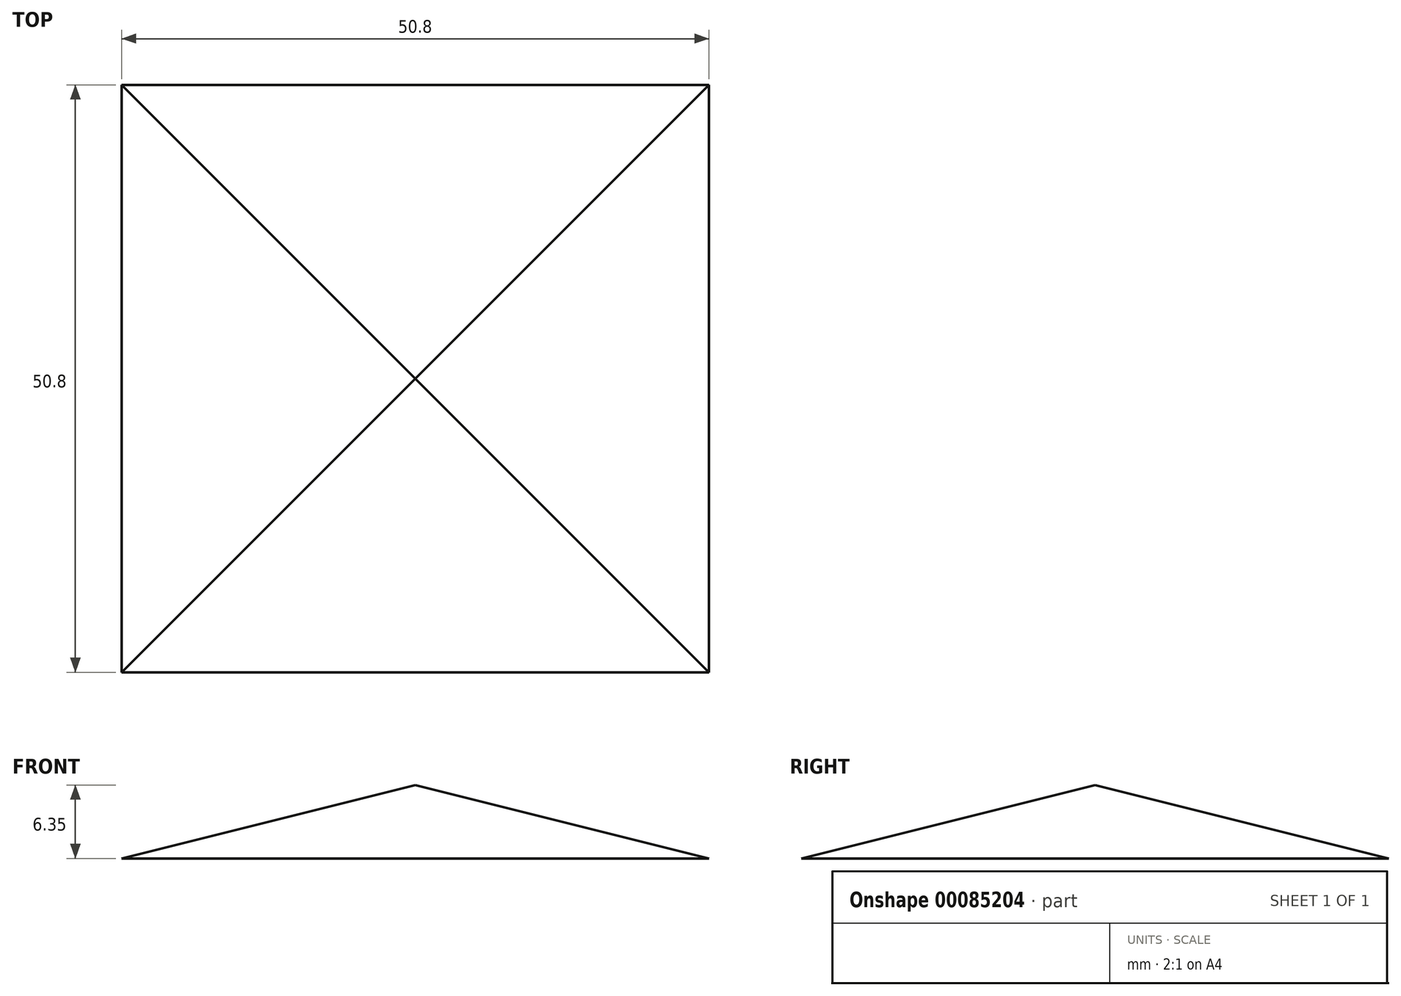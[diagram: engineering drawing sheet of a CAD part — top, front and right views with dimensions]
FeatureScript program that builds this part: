
annotation { "Feature Type Name" : "Feature", "Feature Type Description" : "" }
export const myFeature = defineFeature(function(context is Context, id is Id, definition is map)
    precondition{}
    {
        {
            var Q0;
            Q0=qCreatedBy(makeId("Front.planeOp"),FACE);
            var sketch = newSketch(context, id + "F0", { "sketchPlane" : qUnion([Q0])});
            skLineSegment(sketch, "E0", {"start": v(0, 34.5) * mm, "end": v(0, -30.61) * mm, "construction": true});
            skLineSegment(sketch, "E1", {"start": v(-33.62, 0) * mm, "end": v(36.58, 0) * mm, "construction": true});
            skLineSegment(sketch, "E2.top", {"start": v(-25.4, -3.18) * mm, "end": v(25.4, -3.18) * mm});
            skLineSegment(sketch, "E3", {"start": v(-25.4, -3.18) * mm, "end": v(8.47, 1.06) * mm, "construction": true});
            skLineSegment(sketch, "E4", {"start": v(-8.47, 1.06) * mm, "end": v(25.4, -3.18) * mm, "construction": true});
            skPoint(sketch, "E5", {"position": v(0, 0) * mm});
            skLineSegment(sketch, "E6", {"start": v(-25.4, -3.18) * mm, "end": v(0, 3.17) * mm});
            skLineSegment(sketch, "E7.MirrorCS", {"start": v(25.4, -3.17) * mm, "end": v(0, 3.17) * mm});
            skPoint(sketch, "E8.orphan", {"position": v(25.4, 3.17) * mm});
            skPoint(sketch, "E9.orphan", {"position": v(-25.4, 3.17) * mm});
            skSolve(sketch);
        }
        {
            var Q0;
            Q0 = qSketchRegion(id + "F0", true);
            extrude(context, id + "F1", {"entities" : qUnion([Q0]), "endBound" : BoundingType.SYMMETRIC, "depth" : 50.8 * mm});
        }
        {
            var Q0;
            Q0=qCreatedBy(makeId("Right.planeOp"),FACE);
            cPlane(context, id + "F2", {"entities" : qUnion([Q0]), "cplaneType" : CPlaneType.OFFSET, "offset" : 25.4 * mm, "width" : 152.4 * mm, "height" : 152.4 * mm});
        }
        {
            var Q0;
            Q0=qCreatedBy(id+"F2.planeOp",FACE);
            var sketch = newSketch(context, id + "F3", { "sketchPlane" : qUnion([Q0])});
            skLineSegment(sketch, "E10", {"start": v(0, 4.3) * mm, "end": v(0, -9.26) * mm, "construction": true});
            skLineSegment(sketch, "E11", {"start": v(-21, 0) * mm, "end": v(21.16, 0) * mm, "construction": true});
            skLineSegment(sketch, "E12.bottom", {"start": v(-25.4, 3.18) * mm, "end": v(25.4, 3.18) * mm});
            skLineSegment(sketch, "E12.top", {"start": v(-25.4, -3.17) * mm, "end": v(25.4, -3.17) * mm});
            skLineSegment(sketch, "E12.left", {"start": v(-25.4, 3.18) * mm, "end": v(-25.4, -3.17) * mm});
            skLineSegment(sketch, "E12.right", {"start": v(25.4, 3.18) * mm, "end": v(25.4, -3.17) * mm});
            skLineSegment(sketch, "E13", {"start": v(-25.4, -3.18) * mm, "end": v(25.4, 3.18) * mm, "construction": true});
            skLineSegment(sketch, "E14", {"start": v(-25.4, 3.18) * mm, "end": v(25.4, -3.18) * mm, "construction": true});
            skPoint(sketch, "E15", {"position": v(0, 0) * mm});
            skLineSegment(sketch, "E16", {"start": v(-25.4, -3.17) * mm, "end": v(0, 3.17) * mm});
            skLineSegment(sketch, "E17", {"start": v(0, 3.18) * mm, "end": v(25.4, -3.17) * mm});
            skSolve(sketch);
        }
        {
            var Q0;
            {var subQ0=sQuery(id+"F3.wireOp",EDGE,"E12.left");Q0=makeQuery(id+"F3.imprint","IMPRINT",FACE,{"disambiguationData":[TD([[makeQuery(id+"F3.imprint","IMPRINT",EDGE,{"derivedFrom":subQ0}),1.0]])]});}
            var Q1;
            {var subQ0=sQuery(id+"F3.wireOp",EDGE,"E12.right");Q1=makeQuery(id+"F3.imprint","IMPRINT",FACE,{"disambiguationData":[TD([[makeQuery(id+"F3.imprint","IMPRINT",EDGE,{"derivedFrom":subQ0}),-1.0]])]});}
            extrude(context, id + "F4", {"entities" : qUnion([Q0, Q1]), "operationType" : NewBodyOperationType.REMOVE, "endBound" : BoundingType.THROUGH_ALL, "oppositeDirection" : true, "depth" : 50.8 * mm});
        }
    });
